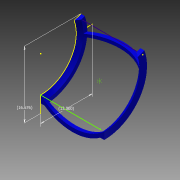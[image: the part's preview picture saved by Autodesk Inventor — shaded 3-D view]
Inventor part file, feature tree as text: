
AUTODESK INVENTOR PART (.ipt)
format: ipt  version: 2014 (Build 180170000, 170)  size: 168,960 bytes
history: native  units: in
note: dims shown in document units (in); Inventor stores cm internally (conversion verified against a paired STEP export)
features: sketch x7, revolve x3, plane x2, hole x2, projected_geometry x2
ambient origin geometry x8: Origin, YZ Plane, XZ Plane, XY Plane, X Axis, Y Axis, Z Axis, Center Point
bodies: Solid1 (feature_tree)
feature tree (16):
  revolve  "Revolution1"  [1 undecoded]
  revolve  "Revolution2"  [1 undecoded]
  plane  "Work Plane1"
  plane  "Work Plane2"
  revolve  "Revolution4"  [1 undecoded]
  sketch  "Sketch6"  dims[d30=12.0in d31=12.0in]
  hole  "Hole3"  [1 undecoded]
  hole  "Hole4"  [1 undecoded]
  sketch  "3D Sketch1"
  sketch  "3D Sketch2"
  sketch  "Sketch7"  dims[d32=0.0275in d33=0.5in d34=0.25in d35=0.75in d36=0.375in d37=0.25in d38=0.5635in d39=1.0in d40=0.8108in d41=0.25in d42=0.75in d43=0.375in d44=0.25in d45=0.5635in d46=1.0in d47=0.8108in d48=16.6756in d49=13.0in]
  sketch  "Sketch1"  dims[d1=12.0in d3=12.0in]
  sketch  "Sketch2"  dims[d5=0.7559in d6=12.0in]
  projected_geometry  "Projected Loop1"
  sketch  "Sketch5"  dims[d8=0.0275in d9=12.0in]
  projected_geometry  "Project Cut Edges2"
note: 5 required parameter values undecoded (feature->parameter linkage not recoverable at this tier; creation-order binding heuristic only, values carry confidence <= 0.55)